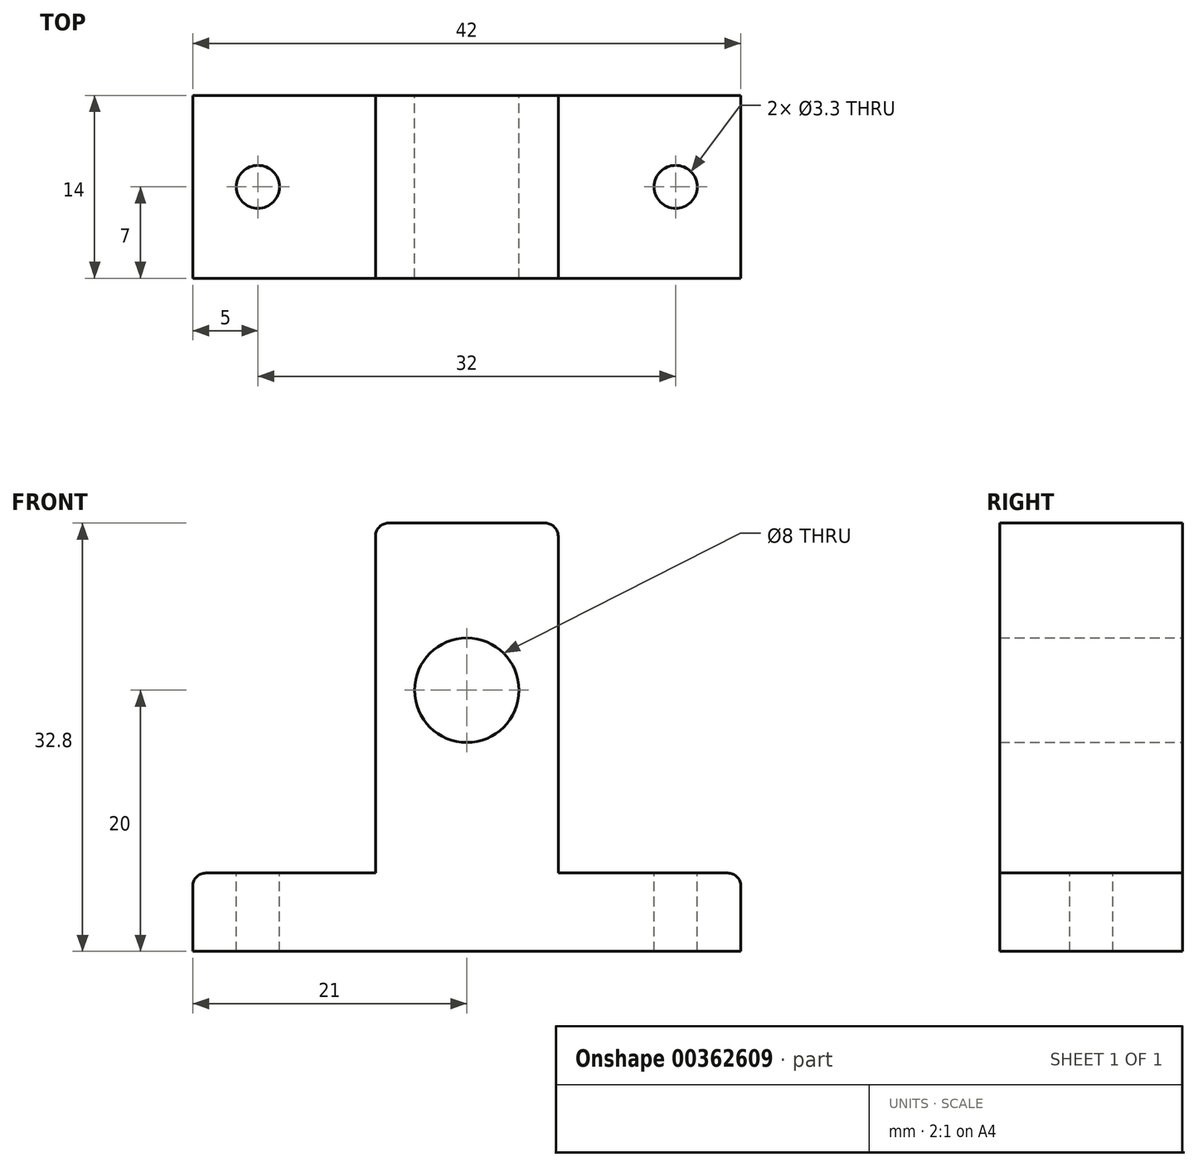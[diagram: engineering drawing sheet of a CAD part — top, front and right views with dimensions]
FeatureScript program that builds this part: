
annotation { "Feature Type Name" : "Feature", "Feature Type Description" : "" }
export const myFeature = defineFeature(function(context is Context, id is Id, definition is map)
    precondition{}
    {
        {
            var Q0;
            Q0=qCreatedBy(makeId("Front.planeOp"),FACE);
            var sketch = newSketch(context, id + "F0", { "sketchPlane" : qUnion([Q0])});
            skCircle(sketch, "E0", {"center": v(0, 0) * mm, "radius": 4 * mm});
            skLineSegment(sketch, "E1.0", {"start": v(7, -14) * mm, "end": v(7, 11.8) * mm});
            skLineSegment(sketch, "E2.0", {"start": v(-7, -14) * mm, "end": v(-7, 11.8) * mm});
            skLineSegment(sketch, "E3.0", {"start": v(21, -20) * mm, "end": v(21, -15) * mm});
            skLineSegment(sketch, "E4.0", {"start": v(-21, -20) * mm, "end": v(-21, -15) * mm});
            skLineSegment(sketch, "E5.0", {"start": v(-21, -20) * mm, "end": v(21, -20) * mm});
            skLineSegment(sketch, "E6.0", {"start": v(-20, -14) * mm, "end": v(-7, -14) * mm});
            skLineSegment(sketch, "E7.trimOffspring", {"start": v(-6, 12.8) * mm, "end": v(6, 12.8) * mm});
            skLineSegment(sketch, "E8.trimOffspring", {"start": v(7, -14) * mm, "end": v(20, -14) * mm});
            skPoint(sketch, "E9.visualSharp", {"position": v(-21, -14) * mm});
            skArc(sketch, "E9.filletArc", {"start": v(-20, -14) * mm, "mid": v(-20.7, -14.3) * mm, "end": v(-21, -15) * mm});
            skPoint(sketch, "E10.visualSharp", {"position": v(21, -14) * mm});
            skArc(sketch, "E10.filletArc", {"start": v(21, -15) * mm, "mid": v(20.7, -14.3) * mm, "end": v(20, -14) * mm});
            skPoint(sketch, "E11.visualSharp", {"position": v(7, 12.8) * mm});
            skArc(sketch, "E11.filletArc", {"start": v(7, 11.8) * mm, "mid": v(6.7, 12.5) * mm, "end": v(6, 12.8) * mm});
            skPoint(sketch, "E12.visualSharp", {"position": v(-7, 12.8) * mm});
            skArc(sketch, "E12.filletArc", {"start": v(-6, 12.8) * mm, "mid": v(-6.7, 12.5) * mm, "end": v(-7, 11.8) * mm});
            skSolve(sketch);
        }
        {
            var Q0;
            Q0 = qSketchRegion(id + "F0", true);
            extrude(context, id + "F1", {"entities" : qUnion([Q0]), "depth" : 14 * mm});
        }
        {
            var Q0;
            Q0=qCreatedBy(makeId("Top.planeOp"),FACE);
            var sketch = newSketch(context, id + "F2", { "sketchPlane" : qUnion([Q0])});
            skPoint(sketch, "E13", {"position": v(-16, -7) * mm});
            skPoint(sketch, "E14", {"position": v(16, -7) * mm});
            skSolve(sketch);
        }
        {
            var Q0;
            Q0=sQuery(id+"F2.wireOp",VERTEX,"E13");
            var Q1;
            Q1=sQuery(id+"F2.wireOp",VERTEX,"E14");
            var Q2;
            Q2=makeQuery(id+"F1.opExtrude","SWEPT_BODY",BODY,{"disambiguationData":[OSD([sQuery(id+"F0.wireOp",EDGE,"E0"),sQuery(id+"F0.wireOp",EDGE,"E1.0"),sQuery(id+"F0.wireOp",EDGE,"E2.0"),sQuery(id+"F0.wireOp",EDGE,"E3.0"),sQuery(id+"F0.wireOp",EDGE,"E4.0"),sQuery(id+"F0.wireOp",EDGE,"E5.0"),sQuery(id+"F0.wireOp",EDGE,"E6.0"),sQuery(id+"F0.wireOp",EDGE,"E7.trimOffspring"),sQuery(id+"F0.wireOp",EDGE,"E8.trimOffspring"),sQuery(id+"F0.wireOp",EDGE,"E9.filletArc"),sQuery(id+"F0.wireOp",EDGE,"E10.filletArc"),sQuery(id+"F0.wireOp",EDGE,"E11.filletArc"),sQuery(id+"F0.wireOp",EDGE,"E12.filletArc")])]});
            hole(context, id + "F3", {"style" : HoleStyle.SIMPLE, "endStyle" : HoleEndStyle.THROUGH, "holeDiameter" : 3.3 * mm, "isTappedThrough" : true, "tappedDepth" : 12 * mm, "tapClearance" : 3, "locations" : qUnion([Q0, Q1]), "scope" : qUnion([Q2])});
        }
    });
